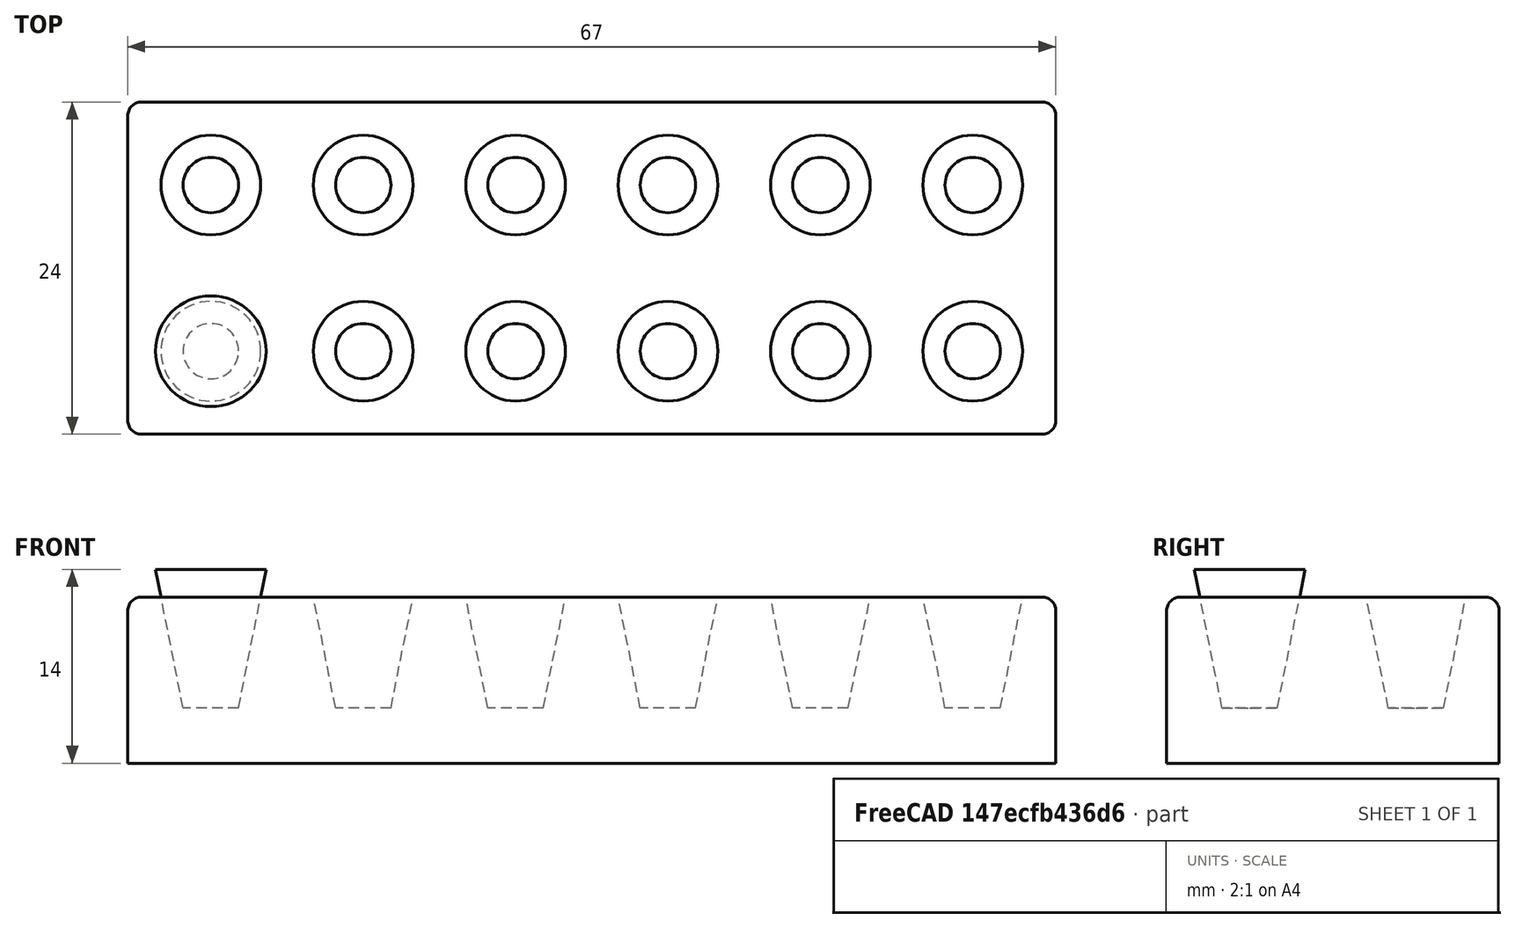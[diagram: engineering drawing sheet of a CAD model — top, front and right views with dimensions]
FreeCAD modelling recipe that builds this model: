
FCSTD DOCUMENT  (FreeCAD 0.21R33694 (Git))
Label: gcasna_repte02
License: All rights reserved
LicenseURL: http://en.wikipedia.org/wiki/All_rights_reserved
objects: Part::Box×1, Part::Cone×1, Part::FeaturePython×1, Part::Fillet×1, Part::Cut×1
note: 4 computed .brp shape members not serialized (recipe doc carries the construction recipe); baked Part::Feature solids carry a one-line shape summary decoded from their .brp

FEATURE [Part::Box] Box  label="Cube"
  AttacherType = Attacher::AttachEngine3D
  Height = 12
  Length = 67
  Width = 24
FEATURE [Part::Cone] Cone
  Angle = 360
  AttacherType = Attacher::AttachEngine3D
  Height = 10
  Placement = pos=(6,6,4) rot=(0,0,1;0rad)
  Radius1 = 2
  Radius2 = 4
FEATURE [Part::FeaturePython] Array  # Draft array (typed FeaturePython)
  AlwaysSyncPlacement = false
  Angle = 360
  ArrayType = 0
  Axis = (0,0,1)
  Base = -> Cone
  Center = (0,0,0)
  Count = 12
  ExpandArray = false
  Fuse = false
  IntervalAxis = (0,0,0)
  IntervalX = (11,0,0)
  IntervalY = (0,12,0)
  IntervalZ = (0,0,100)
  NumberCircles = 3
  NumberPolar = 5
  NumberX = 6
  NumberY = 2
  NumberZ = 1
  PlacementList = 12 placements: [(6,6,4),(6,18,4),(17,6,4),(17,18,4),(28,6,4),(28,18,4),(39,6,4),(39,18,4),(50,6,4),(50,18,4),(61,6,4),(61,18,4)]
  RadialDistance = 50
  ScaleList = (12) [(1,1,1),(1,1,1),(1,1,1),(1,1,1),(1,1,1),(1,1,1),(1,1,1),(1,1,1),(1,1,1),(1,1,1),(1,1,1),(1,1,1)]
  Symmetry = 1
  TangentialDistance = 25
FEATURE [Part::Fillet] Fillet
  Base = -> Box
  Edges = 8 edges r=1: [Edge1,Edge2,Edge3,Edge5,Edge6,Edge7,Edge10,Edge12]
FEATURE [Part::Cut] Cut
  Base = -> Fillet
  Refine = true
  Tool = -> Array
